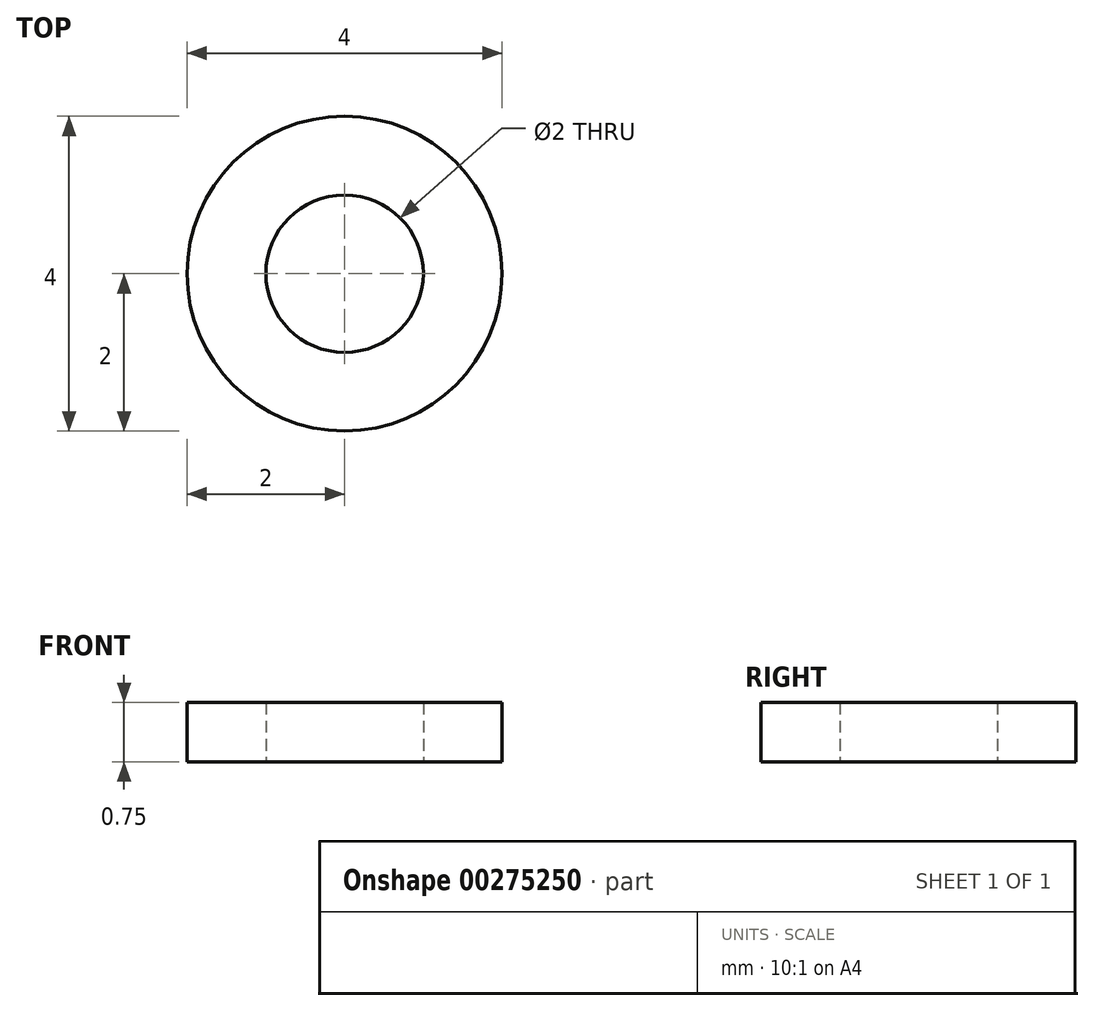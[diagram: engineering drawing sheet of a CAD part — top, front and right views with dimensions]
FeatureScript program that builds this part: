
annotation { "Feature Type Name" : "Feature", "Feature Type Description" : "" }
export const myFeature = defineFeature(function(context is Context, id is Id, definition is map)
    precondition{}
    {
        {
            var Q0;
            Q0=qCreatedBy(makeId("Top.planeOp"),FACE);
            var sketch = newSketch(context, id + "F0", { "sketchPlane" : qUnion([Q0])});
            skCircle(sketch, "E0", {"center": v(0, 0) * mm, "radius": 1 * mm});
            skCircle(sketch, "E1", {"center": v(0, 0) * mm, "radius": 2 * mm});
            skSolve(sketch);
        }
        {
            var Q0;
            Q0=makeQuery(id+"F0.imprint","IMPRINT",FACE,{"disambiguationData":[TD([[makeQuery(id+"F0.imprint","IMPRINT",EDGE,{"derivedFrom":sQuery(id+"F0.wireOp",EDGE,"E0")}),-1.0]])]});
            extrude(context, id + "F1", {"entities" : qUnion([Q0]), "depth" : .75 * mm});
        }
    });
